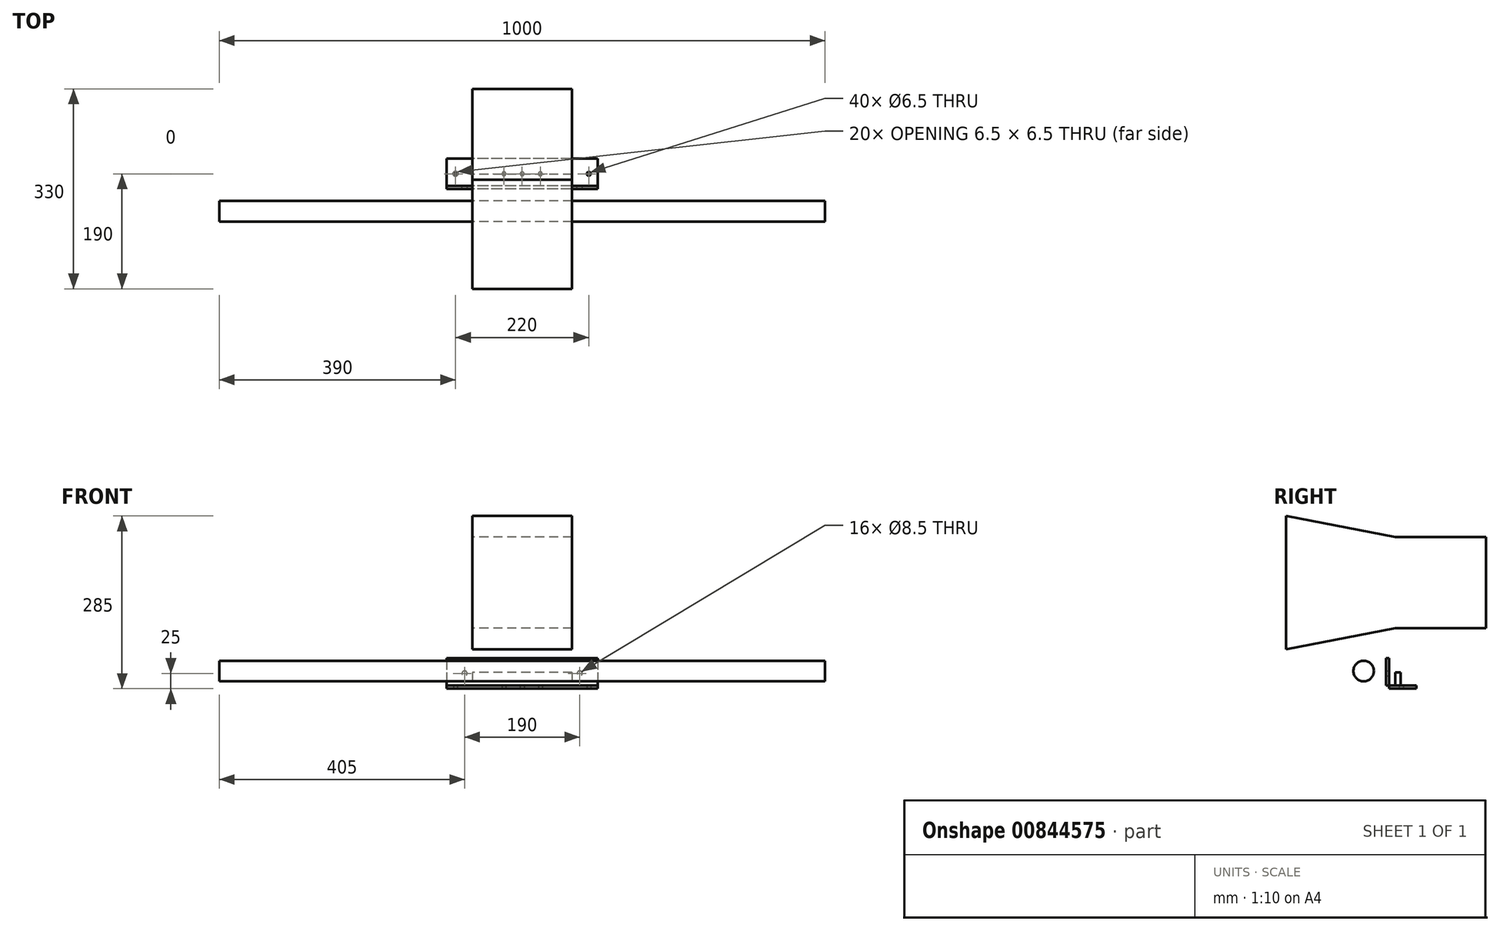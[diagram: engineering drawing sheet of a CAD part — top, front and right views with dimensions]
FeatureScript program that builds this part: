
annotation { "Feature Type Name" : "Feature", "Feature Type Description" : "" }
export const myFeature = defineFeature(function(context is Context, id is Id, definition is map)
    precondition{}
    {
        {
            var Q0;
            Q0=qCreatedBy(makeId("Top.planeOp"),FACE);
            cPlane(context, id + "F0", {"entities" : qUnion([Q0]), "cplaneType" : CPlaneType.OFFSET, "offset" : 20 * mm, "oppositeDirection" : true, "width" : 150 * mm, "height" : 150 * mm});
        }
        {
            var Q0;
            Q0=qCreatedBy(makeId("Right.planeOp"),FACE);
            var sketch = newSketch(context, id + "F1", { "sketchPlane" : qUnion([Q0])});
            skCircle(sketch, "E0", {"center": v(-17, 39) * mm, "radius": 17 * mm});
            skSolve(sketch);
        }
        {
            var Q0;
            Q0 = qSketchRegion(id + "F1", true);
            extrude(context, id + "F2", {"entities" : qUnion([Q0]), "endBound" : BoundingType.SYMMETRIC, "depth" : 1000 * mm, "offsetDistance" : 25.4 * mm});
        }
        {
            var Q0;
            Q0=qCreatedBy(makeId("Right.planeOp"),FACE);
            var sketch = newSketch(context, id + "F3", { "sketchPlane" : qUnion([Q0])});
            skLineSegment(sketch, "E1.bottom", {"start": v(20, 60) * mm, "end": v(25, 60) * mm});
            skLineSegment(sketch, "E1.top", {"start": v(20, 10) * mm, "end": v(25, 10) * mm});
            skLineSegment(sketch, "E1.left", {"start": v(20, 60) * mm, "end": v(20, 10) * mm});
            skLineSegment(sketch, "E1.right", {"start": v(25, 60) * mm, "end": v(25, 10) * mm});
            skLineSegment(sketch, "E2.bottom", {"start": v(20, 10) * mm, "end": v(70, 10) * mm});
            skLineSegment(sketch, "E2.top", {"start": v(20, 15) * mm, "end": v(70, 15) * mm});
            skLineSegment(sketch, "E2.left", {"start": v(20, 10) * mm, "end": v(20, 15) * mm});
            skLineSegment(sketch, "E2.right", {"start": v(70, 10) * mm, "end": v(70, 15) * mm});
            skLineSegment(sketch, "E3.bottom", {"start": v(35, 110) * mm, "end": v(185, 110) * mm});
            skLineSegment(sketch, "E3.top", {"start": v(35, 260) * mm, "end": v(185, 260) * mm});
            skLineSegment(sketch, "E3.left", {"start": v(35, 110) * mm, "end": v(35, 260) * mm});
            skLineSegment(sketch, "E3.right", {"start": v(185, 110) * mm, "end": v(185, 260) * mm});
            skLineSegment(sketch, "E4.bottom", {"start": v(35, 110) * mm, "end": v(60, 110) * mm});
            skLineSegment(sketch, "E4.top", {"start": v(35, 15.1) * mm, "end": v(60, 15.1) * mm});
            skLineSegment(sketch, "E4.left", {"start": v(35, 110) * mm, "end": v(35, 15.1) * mm});
            skLineSegment(sketch, "E4.right", {"start": v(60, 110) * mm, "end": v(60, 15.1) * mm});
            skLineSegment(sketch, "E5", {"start": v(35, 110) * mm, "end": v(-145, 75) * mm});
            skLineSegment(sketch, "E6", {"start": v(-145, 75) * mm, "end": v(-145, 295) * mm});
            skLineSegment(sketch, "E7", {"start": v(-145, 295) * mm, "end": v(35, 260) * mm});
            skLineSegment(sketch, "E8.bottom", {"start": v(28.06, -20) * mm, "end": v(60.3, -20) * mm});
            skLineSegment(sketch, "E8.top", {"start": v(28.06, -8) * mm, "end": v(60.3, -8) * mm});
            skLineSegment(sketch, "E8.left", {"start": v(28.06, -20) * mm, "end": v(28.06, -8) * mm});
            skLineSegment(sketch, "E8.right", {"start": v(60.3, -20) * mm, "end": v(60.3, -8) * mm});
            skPoint(sketch, "E9.oppositeSnap0", {"position": v(44.18, -8) * mm});
            skLineSegment(sketch, "E9.bottom", {"start": v(34.18, -8) * mm, "end": v(44.18, -8) * mm});
            skLineSegment(sketch, "E9.top", {"start": v(34.18, 37) * mm, "end": v(44.18, 37) * mm});
            skLineSegment(sketch, "E9.left", {"start": v(34.18, -8) * mm, "end": v(34.18, 37) * mm});
            skLineSegment(sketch, "E9.right", {"start": v(44.18, -8) * mm, "end": v(44.18, 37) * mm});
            skSolve(sketch);
        }
        {
            var Q0;
            {var subQ0=sQuery(id+"F3.wireOp",EDGE,"E1.bottom");Q0=makeQuery(id+"F3.imprint","IMPRINT",FACE,{"disambiguationData":[TD([[makeQuery(id+"F3.imprint","IMPRINT",EDGE,{"derivedFrom":subQ0}),-1.0]])]});}
            var Q1;
            {var subQ5=sQuery(id+"F3.wireOp",EDGE,"E2.left");Q1=makeQuery(id+"F3.imprint","IMPRINT",FACE,{"disambiguationData":[TD([[makeQuery(id+"F3.imprint","IMPRINT",EDGE,{"derivedFrom":subQ5}),-1.0]])]});}
            var Q2;
            {var subQ6=sQuery(id+"F3.wireOp",EDGE,"E2.right");Q2=makeQuery(id+"F3.imprint","IMPRINT",FACE,{"disambiguationData":[TD([[makeQuery(id+"F3.imprint","IMPRINT",EDGE,{"derivedFrom":subQ6}),1.0]])]});}
            var Q3;
            {var subQ0=sQuery(id+"F3.wireOp",EDGE,"E2.bottom");var subQ1=sQuery(id+"F3.wireOp",EDGE,"E1.right");var subQ2=makeQuery(id+"F3.imprint","INTERSECT",VERTEX,{"derivedFrom":[subQ1,subQ0]});Q3=makeQuery(id+"F3.imprint","IMPRINT",FACE,{"disambiguationData":[TD([[makeQuery(id+"F3.imprint","IMPRINT",EDGE,{"disambiguationData":[TD([[subQ2,1.0]])],"derivedFrom":subQ1}),1.0]])]});}
            var Q4;
            {var subQ0=sQuery(id+"F3.wireOp",EDGE,"E9.left");var subQ1=sQuery(id+"F3.wireOp",EDGE,"E2.bottom");var subQ2=makeQuery(id+"F3.imprint","INTERSECT",VERTEX,{"derivedFrom":[subQ1,subQ0]});Q4=makeQuery(id+"F3.imprint","IMPRINT",FACE,{"disambiguationData":[TD([[makeQuery(id+"F3.imprint","IMPRINT",EDGE,{"disambiguationData":[TD([[subQ2,-1.0]])],"derivedFrom":subQ1}),1.0]])]});}
            extrude(context, id + "F4", {"entities" : qUnion([Q0, Q1, Q2, Q3, Q4]), "endBound" : BoundingType.SYMMETRIC, "depth" : 250 * mm, "offsetDistance" : 25 * mm});
        }
        {
            var Q0;
            Q0=makeQuery(id+"F3.imprint","IMPRINT",FACE,{"disambiguationData":[TD([[makeQuery(id+"F3.imprint","IMPRINT",EDGE,{"derivedFrom":sQuery(id+"F3.wireOp",EDGE,"E3.left")}),1.0]])]});
            var Q1;
            Q1=makeQuery(id+"F3.imprint","IMPRINT",FACE,{"disambiguationData":[TD([[makeQuery(id+"F3.imprint","IMPRINT",EDGE,{"derivedFrom":sQuery(id+"F3.wireOp",EDGE,"E3.bottom")}),1.0]])]});
            var Q2;
            Q2=makeQuery(id+"F3.imprint","IMPRINT",FACE,{"disambiguationData":[TD([[makeQuery(id+"F3.imprint","IMPRINT",EDGE,{"derivedFrom":sQuery(id+"F3.wireOp",EDGE,"E4.bottom")}),-1.0]])]});
            var Q3;
            {var subQ5=sQuery(id+"F3.wireOp",EDGE,"E9.top");Q3=makeQuery(id+"F3.imprint","IMPRINT",FACE,{"disambiguationData":[TD([[makeQuery(id+"F3.imprint","IMPRINT",EDGE,{"derivedFrom":subQ5}),-1.0]])]});}
            extrude(context, id + "F5", {"entities" : qUnion([Q0, Q1, Q2, Q3]), "operationType" : NewBodyOperationType.ADD, "endBound" : BoundingType.SYMMETRIC, "depth" : 165 * mm, "offsetDistance" : 25 * mm});
        }
        {
            var Q0;
            Q0=makeQuery(id+"F4.opExtrude","SWEPT_FACE",FACE,{"disambiguationData":[OSD([sQuery(id+"F3.wireOp",EDGE,"E2.bottom")])]});
            var sketch = newSketch(context, id + "F6", { "sketchPlane" : qUnion([Q0])});
            skCircle(sketch, "E10", {"center": v(110, -45) * mm, "radius": 2.5 * mm});
            skCircle(sketch, "E11", {"center": v(-110, -45) * mm, "radius": 2.5 * mm});
            skCircle(sketch, "E12", {"center": v(0, -45) * mm, "radius": 2.5 * mm});
            skPoint(sketch, "E13", {"position": v(30, -45) * mm});
            skPoint(sketch, "E14", {"position": v(-30, -45) * mm});
            skSolve(sketch);
        }
        {
            var Q0;
            Q0=sQuery(id+"F6.wireOp",VERTEX,"E10.center");
            var Q1;
            Q1=sQuery(id+"F6.wireOp",VERTEX,"E12.center");
            var Q2;
            Q2=sQuery(id+"F6.wireOp",VERTEX,"E11.center");
            var Q3;
            Q3=sQuery(id+"F6.wireOp",VERTEX,"E13");
            var Q4;
            Q4=sQuery(id+"F6.wireOp",VERTEX,"E14");
            var Q5;
            Q5=makeQuery(id+"F4.opExtrude","SWEPT_BODY",BODY,{"disambiguationData":[OSD([sQuery(id+"F3.wireOp",EDGE,"E1.bottom"),sQuery(id+"F3.wireOp",EDGE,"E1.left"),sQuery(id+"F3.wireOp",EDGE,"E1.right"),sQuery(id+"F3.wireOp",EDGE,"E2.bottom"),sQuery(id+"F3.wireOp",EDGE,"E2.top"),sQuery(id+"F3.wireOp",EDGE,"E2.left"),sQuery(id+"F3.wireOp",EDGE,"E2.right"),sQuery(id+"F3.wireOp",EDGE,"E4.top")])]});
            hole(context, id + "F7", {"style" : HoleStyle.SIMPLE, "endStyle" : HoleEndStyle.THROUGH, "holeDiameter" : 6.5 * mm, "majorDiameter" : 5 * mm, "isTappedThrough" : true, "tappedDepth" : 12 * mm, "tapClearance" : 3, "locations" : qUnion([Q0, Q1, Q2, Q3, Q4]), "scope" : qUnion([Q5])});
        }
        {
            var Q0;
            Q0=makeQuery(id+"F4.opExtrude","SWEPT_FACE",FACE,{"disambiguationData":[OSD([sQuery(id+"F3.wireOp",EDGE,"E1.right")])]});
            var sketch = newSketch(context, id + "F8", { "sketchPlane" : qUnion([Q0])});
            skPoint(sketch, "E15", {"position": v(-95, 35) * mm});
            skPoint(sketch, "E16", {"position": v(95, 35) * mm});
            skSolve(sketch);
        }
        {
            var Q0;
            Q0=sQuery(id+"F8.wireOp",VERTEX,"E15");
            var Q1;
            Q1=sQuery(id+"F8.wireOp",VERTEX,"E16");
            var Q2;
            Q2=makeQuery(id+"F4.opExtrude","SWEPT_BODY",BODY,{"disambiguationData":[OSD([sQuery(id+"F3.wireOp",EDGE,"E1.bottom"),sQuery(id+"F3.wireOp",EDGE,"E1.left"),sQuery(id+"F3.wireOp",EDGE,"E1.right"),sQuery(id+"F3.wireOp",EDGE,"E2.bottom"),sQuery(id+"F3.wireOp",EDGE,"E2.top"),sQuery(id+"F3.wireOp",EDGE,"E2.left"),sQuery(id+"F3.wireOp",EDGE,"E2.right"),sQuery(id+"F3.wireOp",EDGE,"E4.top")])]});
            var Q3;
            Q3=makeQuery(id+"F2.opExtrude","SWEPT_BODY",BODY,{"disambiguationData":[OSD([sQuery(id+"F1.wireOp",EDGE,"E0")])]});
            hole(context, id + "F9", {"style" : HoleStyle.SIMPLE, "endStyle" : HoleEndStyle.BLIND, "holeDiameter" : 8.5 * mm, "majorDiameter" : 5 * mm, "holeDepth" : 6 * mm, "isTappedThrough" : true, "tappedDepth" : 12 * mm, "tapClearance" : 3, "locations" : qUnion([Q0, Q1]), "scope" : qUnion([Q2, Q3])});
        }
    });
